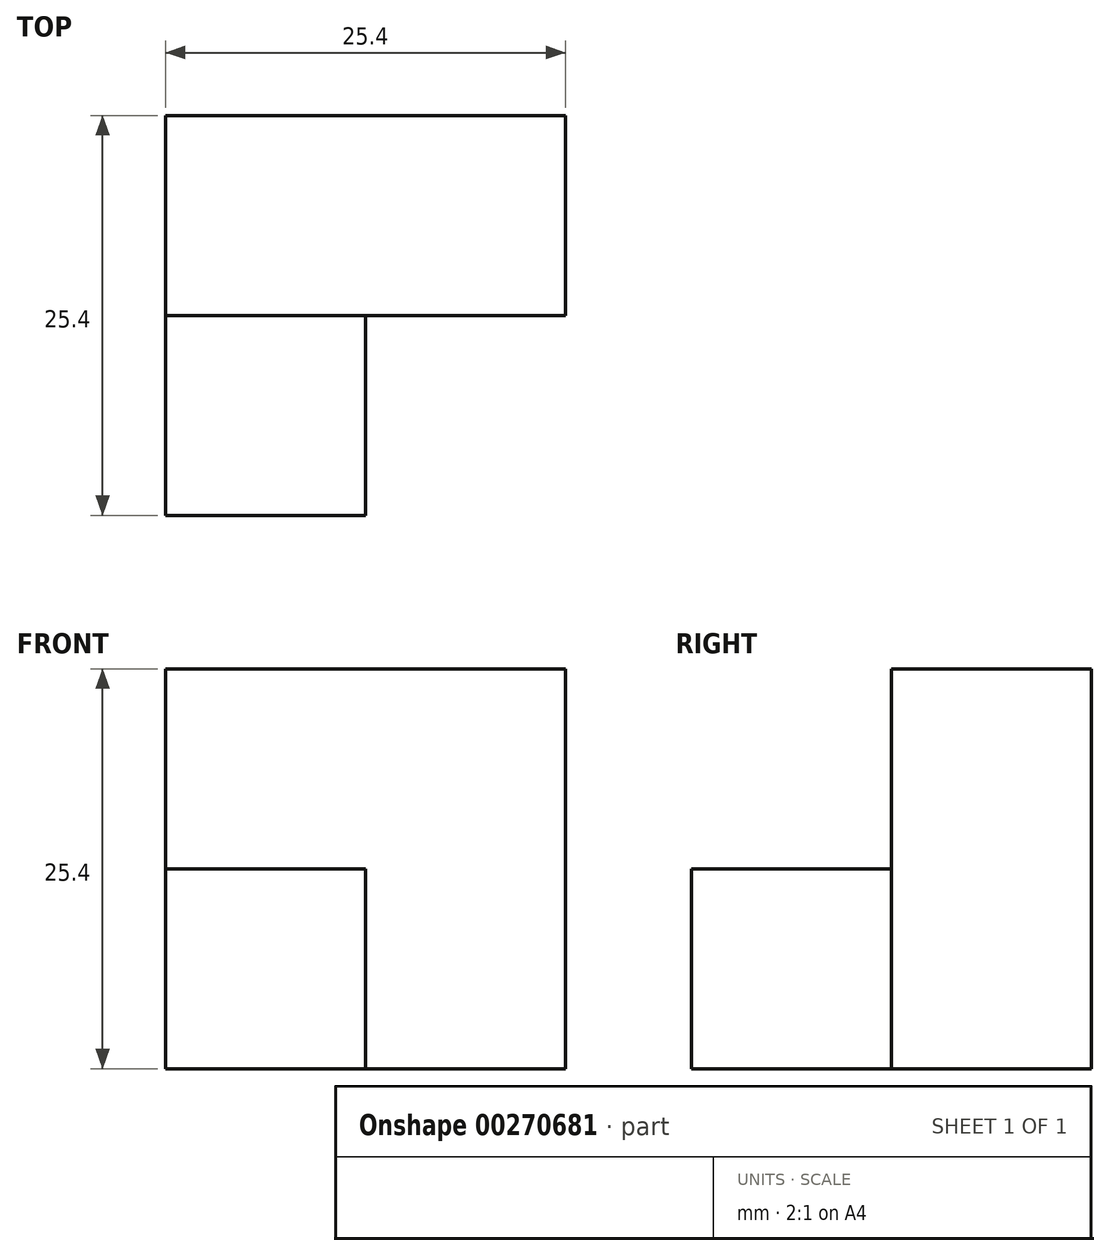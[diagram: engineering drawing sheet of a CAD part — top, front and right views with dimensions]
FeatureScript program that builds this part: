
annotation { "Feature Type Name" : "Feature", "Feature Type Description" : "" }
export const myFeature = defineFeature(function(context is Context, id is Id, definition is map)
    precondition{}
    {
        {
            var Q0;
            Q0=qCreatedBy(makeId("Front.planeOp"),FACE);
            var sketch = newSketch(context, id + "F0", { "sketchPlane" : qUnion([Q0])});
            skLineSegment(sketch, "E0.bottom", {"start": v(0, 0) * mm, "end": v(-25.4, 0) * mm});
            skLineSegment(sketch, "E0.top", {"start": v(0, 25.4) * mm, "end": v(-25.4, 25.4) * mm});
            skLineSegment(sketch, "E0.left", {"start": v(0, 0) * mm, "end": v(0, 25.4) * mm});
            skLineSegment(sketch, "E0.right", {"start": v(-25.4, 0) * mm, "end": v(-25.4, 25.4) * mm});
            skSolve(sketch);
        }
        {
            var Q0;
            Q0=makeQuery(id+"F0.imprint","IMPRINT",FACE,{"disambiguationData":[TD([[makeQuery(id+"F0.imprint","IMPRINT",EDGE,{"derivedFrom":sQuery(id+"F0.wireOp",EDGE,"E0.bottom")}),-1.0]])]});
            extrude(context, id + "F1", {"entities" : qUnion([Q0]), "depth" : 25.4 * mm});
        }
        {
            var Q0;
            Q0=makeQuery(id+"F1.opExtrude","CAP_FACE",FACE,{"disambiguationData":[OSD([sQuery(id+"F0.wireOp",EDGE,"E0.bottom"),sQuery(id+"F0.wireOp",EDGE,"E0.top"),sQuery(id+"F0.wireOp",EDGE,"E0.left"),sQuery(id+"F0.wireOp",EDGE,"E0.right")])],"isStart":false});
            var sketch = newSketch(context, id + "F2", { "sketchPlane" : qUnion([Q0])});
            skLineSegment(sketch, "E1", {"start": v(-25.4, 12.7) * mm, "end": v(-12.7, 12.7) * mm});
            skPoint(sketch, "E1.endSnap0", {"position": v(-12.7, 0) * mm});
            skLineSegment(sketch, "E2", {"start": v(-12.7, 12.7) * mm, "end": v(-12.7, 0) * mm});
            skSolve(sketch);
        }
        {
            var Q0;
            {var subQ3=sQuery(id+"F2.wireOp",EDGE,"E1");Q0=makeQuery(id+"F2.imprint","IMPRINT",FACE,{"disambiguationData":[TD([[makeQuery(id+"F2.imprint","IMPRINT",EDGE,{"derivedFrom":subQ3}),1.0]])]});}
            extrude(context, id + "F3", {"entities" : qUnion([Q0]), "operationType" : NewBodyOperationType.REMOVE, "oppositeDirection" : true, "depth" : 12.7 * mm});
        }
    });
